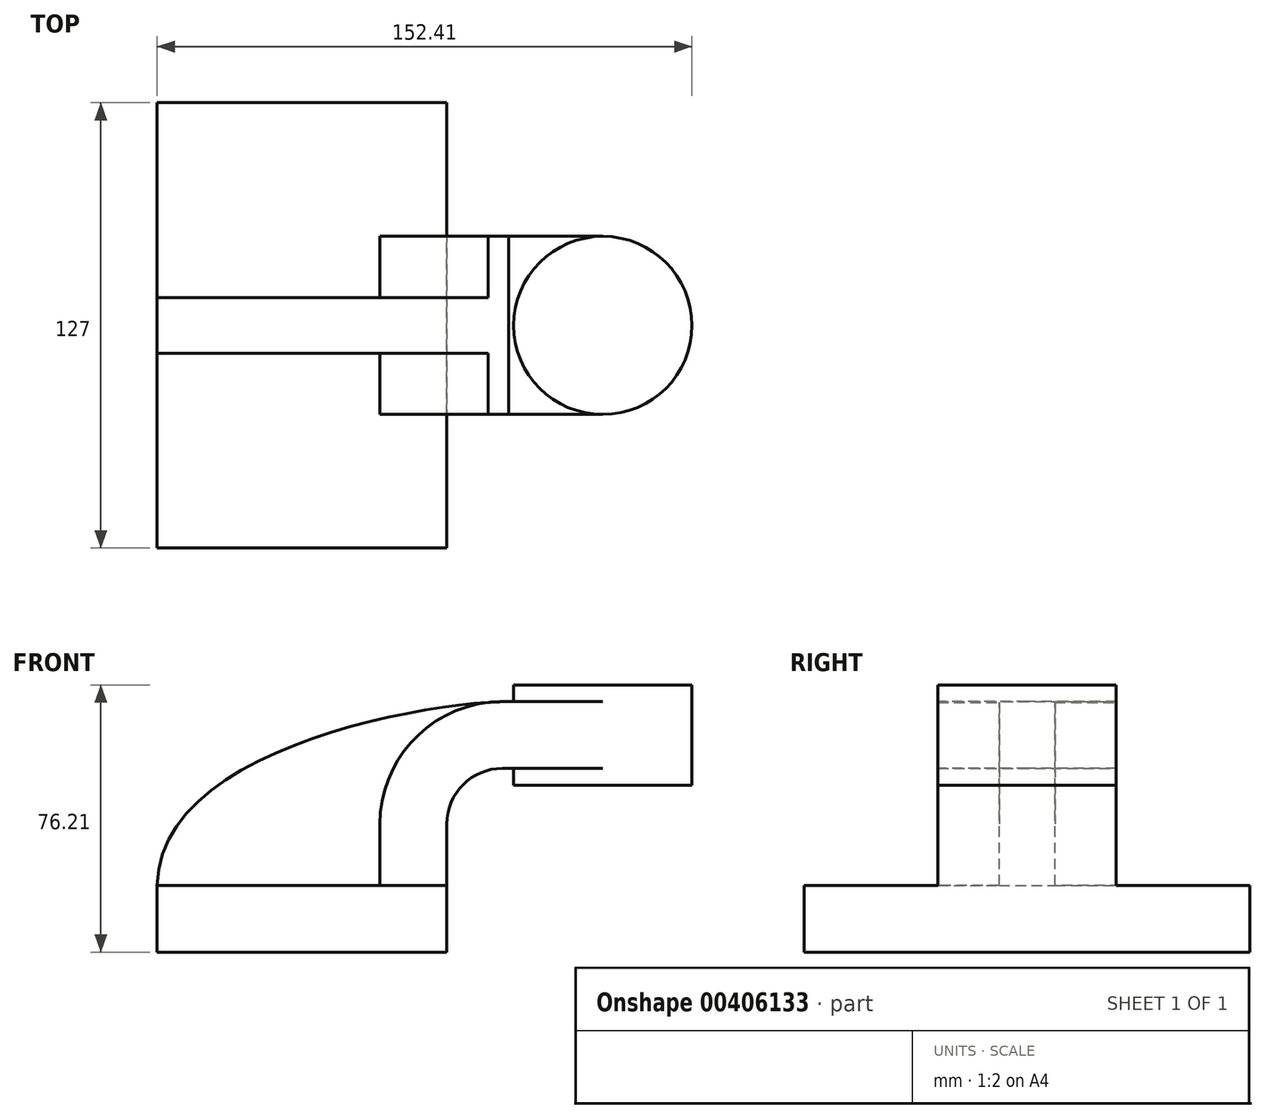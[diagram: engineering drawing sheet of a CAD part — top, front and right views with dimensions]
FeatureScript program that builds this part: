
annotation { "Feature Type Name" : "Feature", "Feature Type Description" : "" }
export const myFeature = defineFeature(function(context is Context, id is Id, definition is map)
    precondition{}
    {
        {
            var Q0;
            Q0=qCreatedBy(makeId("Front.planeOp"),FACE);
            var sketch = newSketch(context, id + "F0", { "sketchPlane" : qUnion([Q0])});
            skLineSegment(sketch, "E0.bottom", {"start": v(-41.27, -9.53) * mm, "end": v(41.28, -9.53) * mm});
            skLineSegment(sketch, "E0.top", {"start": v(-41.28, 9.53) * mm, "end": v(41.28, 9.53) * mm});
            skLineSegment(sketch, "E0.left", {"start": v(-41.28, -9.53) * mm, "end": v(-41.28, 9.53) * mm});
            skLineSegment(sketch, "E0.right", {"start": v(41.28, -9.53) * mm, "end": v(41.28, 9.53) * mm});
            skPoint(sketch, "E0.middle", {"position": v(0, 0) * mm});
            skLineSegment(sketch, "E1.bottom", {"start": v(60.32, 38.1) * mm, "end": v(111.12, 38.1) * mm});
            skLineSegment(sketch, "E1.top", {"start": v(60.32, 66.68) * mm, "end": v(111.12, 66.68) * mm});
            skLineSegment(sketch, "E1.left", {"start": v(60.32, 38.1) * mm, "end": v(60.32, 66.67) * mm});
            skLineSegment(sketch, "E1.right", {"start": v(111.12, 38.1) * mm, "end": v(111.12, 66.67) * mm});
            skPoint(sketch, "E1.middle", {"position": v(85.72, 52.39) * mm});
            skLineSegment(sketch, "E2", {"start": v(41.28, 9.53) * mm, "end": v(41.27, 27) * mm});
            skArc(sketch, "E3", {"start": v(41.27, 27) * mm, "mid": v(45.92, 38.23) * mm, "end": v(57.15, 42.88) * mm});
            skLineSegment(sketch, "E4", {"start": v(57.15, 42.88) * mm, "end": v(85.72, 42.88) * mm});
            skLineSegment(sketch, "E5.0", {"start": v(57.15, 61.93) * mm, "end": v(85.72, 61.93) * mm});
            skArc(sketch, "E5.1", {"start": v(22.23, 27) * mm, "mid": v(32.45, 51.7) * mm, "end": v(57.15, 61.93) * mm});
            skLineSegment(sketch, "E5.2", {"start": v(22.23, 9.52) * mm, "end": v(22.22, 27) * mm});
            skLineSegment(sketch, "E6", {"start": v(85.72, 38.1) * mm, "end": v(85.72, 66.68) * mm});
            skFitSpline(sketch, "E7", {"points": [v(-41.27, 9.53) * mm, v(60.32, 61.93) * mm], "startDerivative": vector(1.5, 118.13) * mm, "endDerivative": vector(71.57, -0.78) * mm});
            skSolve(sketch);
        }
        {
            var Q0;
            Q0=makeQuery(id+"F0.imprint","IMPRINT",FACE,{"disambiguationData":[TD([[makeQuery(id+"F0.imprint","IMPRINT",EDGE,{"derivedFrom":sQuery(id+"F0.wireOp",EDGE,"E0.bottom")}),1.0]])]});
            extrude(context, id + "F1", {"entities" : qUnion([Q0]), "endBound" : BoundingType.SYMMETRIC, "oppositeDirection" : true, "depth" : 127 * mm});
        }
        {
            var Q0;
            {var subQ1=sQuery(id+"F0.wireOp",EDGE,"E2");Q0=makeQuery(id+"F0.imprint","IMPRINT",FACE,{"disambiguationData":[TD([[makeQuery(id+"F0.imprint","IMPRINT",EDGE,{"derivedFrom":subQ1}),1.0]])]});}
            var Q1;
            {var subQ3=sQuery(id+"F0.wireOp",EDGE,"E4");var subQ5=sQuery(id+"F0.wireOp",EDGE,"E6");var subQ6=makeQuery(id+"F0.imprint","INTERSECT",VERTEX,{"derivedFrom":[subQ3,subQ5]});Q1=makeQuery(id+"F0.imprint","IMPRINT",FACE,{"disambiguationData":[TD([[makeQuery(id+"F0.imprint","IMPRINT",EDGE,{"disambiguationData":[TD([[subQ6,1.0]])],"derivedFrom":subQ3}),1.0]])]});}
            extrude(context, id + "F2", {"entities" : qUnion([Q0, Q1]), "operationType" : NewBodyOperationType.ADD, "endBound" : BoundingType.SYMMETRIC, "depth" : 50.8 * mm});
        }
        {
            var Q0;
            {var subQ3=sQuery(id+"F0.wireOp",EDGE,"E5.2");Q0=makeQuery(id+"F0.imprint","IMPRINT",FACE,{"disambiguationData":[TD([[makeQuery(id+"F0.imprint","IMPRINT",EDGE,{"derivedFrom":subQ3}),1.0]])]});}
            extrude(context, id + "F3", {"entities" : qUnion([Q0]), "operationType" : NewBodyOperationType.ADD, "endBound" : BoundingType.SYMMETRIC, "depth" : 15.88 * mm});
        }
        {
            var Q0;
            {var subQ0=sQuery(id+"F0.wireOp",EDGE,"E1.right");Q0=makeQuery(id+"F0.imprint","IMPRINT",FACE,{"disambiguationData":[TD([[makeQuery(id+"F0.imprint","IMPRINT",EDGE,{"derivedFrom":subQ0}),1.0]])]});}
            var Q1;
            Q1=sQuery(id+"F0.wireOp",EDGE,"E6");
            revolve(context, id + "F4", {"operationType" : NewBodyOperationType.ADD, "entities" : qUnion([Q0]), "axis" : qUnion([Q1]), "revolveType" : RevolveType.ONE_DIRECTION, "angle" : 360 * degree});
        }
    });
